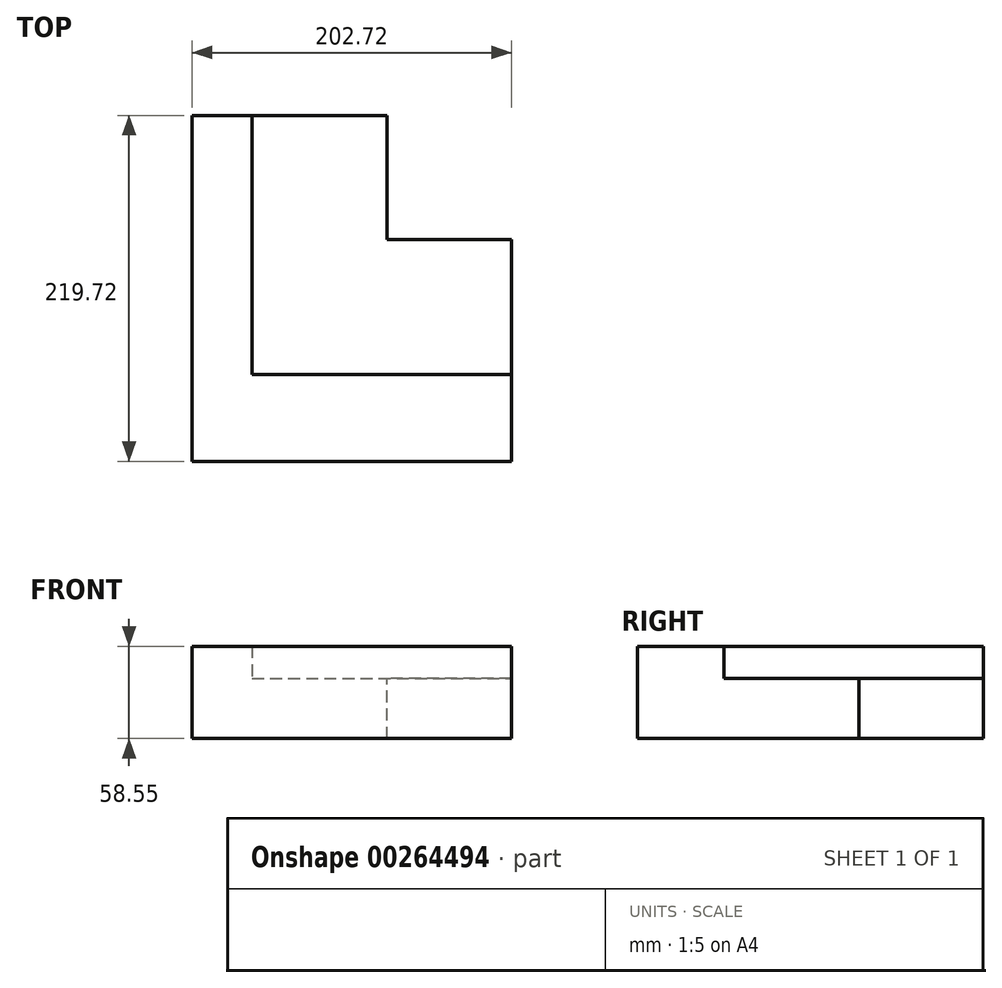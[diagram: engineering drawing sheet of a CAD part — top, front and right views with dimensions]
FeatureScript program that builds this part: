
annotation { "Feature Type Name" : "Feature", "Feature Type Description" : "" }
export const myFeature = defineFeature(function(context is Context, id is Id, definition is map)
    precondition{}
    {
        {
            var Q0;
            Q0=qCreatedBy(makeId("Top.planeOp"),FACE);
            var sketch = newSketch(context, id + "F0", { "sketchPlane" : qUnion([Q0])});
            skLineSegment(sketch, "E0.bottom", {"start": v(-101.36, 110.86) * mm, "end": v(101.36, 110.86) * mm, "construction": true});
            skLineSegment(sketch, "E0.top", {"start": v(-101.36, -110.86) * mm, "end": v(101.36, -110.86) * mm, "construction": true});
            skLineSegment(sketch, "E0.left", {"start": v(-101.36, 110.86) * mm, "end": v(-101.36, -110.86) * mm, "construction": true});
            skLineSegment(sketch, "E0.right", {"start": v(101.36, 110.86) * mm, "end": v(101.36, -110.86) * mm, "construction": true});
            skLineSegment(sketch, "E1", {"start": v(0, 0) * mm, "end": v(0, -110.86) * mm, "construction": true});
            skLineSegment(sketch, "E2", {"start": v(0, 0) * mm, "end": v(101.36, 0) * mm, "construction": true});
            skLineSegment(sketch, "E3", {"start": v(-101.36, 110.86) * mm, "end": v(-63.36, 110.86) * mm});
            skLineSegment(sketch, "E4", {"start": v(-63.36, 110.86) * mm, "end": v(-63.36, -53.86) * mm});
            skLineSegment(sketch, "E5", {"start": v(-63.36, -53.86) * mm, "end": v(101.36, -53.86) * mm});
            skLineSegment(sketch, "E6", {"start": v(101.36, -53.86) * mm, "end": v(101.36, -110.86) * mm});
            skLineSegment(sketch, "E7", {"start": v(-101.36, -110.86) * mm, "end": v(-101.36, 110.86) * mm});
            skLineSegment(sketch, "E8", {"start": v(-101.36, -110.86) * mm, "end": v(101.36, -110.86) * mm});
            skSolve(sketch);
        }
        {
            var Q0;
            Q0 = qSketchRegion(id + "F0", true);
            extrude(context, id + "F1", {"entities" : qUnion([Q0]), "depth" : 20.55 * mm});
        }
        {
            var Q0;
            Q0=makeQuery(id+"F1.opExtrude","CAP_FACE",FACE,{"disambiguationData":[OSD([sQuery(id+"F0.wireOp",EDGE,"E3"),sQuery(id+"F0.wireOp",EDGE,"E4"),sQuery(id+"F0.wireOp",EDGE,"E5"),sQuery(id+"F0.wireOp",EDGE,"E6"),sQuery(id+"F0.wireOp",EDGE,"E7"),sQuery(id+"F0.wireOp",EDGE,"E8")])],"isStart":true});
            var sketch = newSketch(context, id + "F2", { "sketchPlane" : qUnion([Q0])});
            skLineSegment(sketch, "E9", {"start": v(101.36, 110.86) * mm, "end": v(101.36, -31.86) * mm});
            skLineSegment(sketch, "E10", {"start": v(101.36, -31.86) * mm, "end": v(22.36, -31.86) * mm});
            skLineSegment(sketch, "E11", {"start": v(22.36, -31.86) * mm, "end": v(22.36, -110.86) * mm});
            skLineSegment(sketch, "E12", {"start": v(22.36, -110.86) * mm, "end": v(-101.36, -110.86) * mm});
            skLineSegment(sketch, "E13", {"start": v(-101.36, -110.86) * mm, "end": v(-101.36, 110.86) * mm});
            skLineSegment(sketch, "E14", {"start": v(-101.36, 110.86) * mm, "end": v(101.36, 110.86) * mm});
            skSolve(sketch);
        }
        {
            var Q0;
            Q0 = qSketchRegion(id + "F2", true);
            extrude(context, id + "F3", {"entities" : qUnion([Q0]), "operationType" : NewBodyOperationType.ADD, "depth" : 38 * mm});
        }
        {
            var Q0;
            Q0=makeQuery(id+"F1.opExtrude","CAP_FACE",FACE,{"disambiguationData":[OSD([sQuery(id+"F0.wireOp",EDGE,"E3"),sQuery(id+"F0.wireOp",EDGE,"E4"),sQuery(id+"F0.wireOp",EDGE,"E5"),sQuery(id+"F0.wireOp",EDGE,"E6"),sQuery(id+"F0.wireOp",EDGE,"E7"),sQuery(id+"F0.wireOp",EDGE,"E8")])],"isStart":false});
            var sketch = newSketch(context, id + "F4", { "sketchPlane" : qUnion([Q0])});
            skLineSegment(sketch, "E15.bottom", {"start": v(-101.36, -110.86) * mm, "end": v(101.36, -110.86) * mm});
            skLineSegment(sketch, "E15.top", {"start": v(-101.36, -108.86) * mm, "end": v(101.36, -108.86) * mm});
            skLineSegment(sketch, "E15.left", {"start": v(-101.36, -110.86) * mm, "end": v(-101.36, -108.86) * mm});
            skLineSegment(sketch, "E15.right", {"start": v(101.36, -110.86) * mm, "end": v(101.36, -108.86) * mm});
            skSolve(sketch);
        }
        {
            var Q0;
            Q0 = qSketchRegion(id + "F4", true);
            extrude(context, id + "F5", {"entities" : qUnion([Q0]), "operationType" : NewBodyOperationType.REMOVE, "endBound" : BoundingType.THROUGH_ALL, "oppositeDirection" : true, "depth" : 25 * mm});
        }
    });
